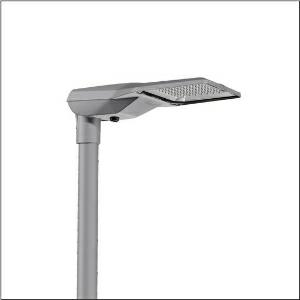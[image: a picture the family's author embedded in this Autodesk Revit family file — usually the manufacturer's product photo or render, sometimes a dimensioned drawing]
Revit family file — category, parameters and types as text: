
# Revit family: streetlight_sl_21_iq_midi___p0_5a_5xe3v31u08mb_699d
name_source: partatom
category: Lighting Fixtures
units: mm (PartAtom-declared; Revit-internal decimal feet)

## family parameters
Cut with Voids When Loaded = No
Host = Face
Light Source = No
Part Type = Normal
Room Calculation Point = No
Round Connector Dimension = Use Diameter
Shared = No

## types (1)
- --- (1 x LED, 18020 lm, 129.3 W, 3000K)
    Apparent Load = 129 VA
    CIE Flux Codes = 37 73 96 100 100
    Color Rendering = 70
    Color Temperature = 3000K
    Default Elevation = 1800 mm
    Description = Streetlight SL 21 iQ midi, mast luminaire, primary light control with lens, of PMMA, primary optical cover: cover, of toughened safety glass, transparent, light distribution: P0.5a, light emission: direct distribution, primary light characteristic: asymmetric, installation type: post-top, side-entry, LED, High Power LED, rated luminous flux: 18.020lm, luminous efficacy: 139lm/W, light colour: 730, colour temperature: 3000K, control gear: iQ-Street Remote, D4i with power reduction, control: pre-setting: logarithmic dimming characteristic, Street-Remote, Auto-Match, Temp-Guard, Lumen-Switch, Night-Set, Smart-Wire, Light-Fading, Desk-Remote (wireless, voltage-free reading and setting of iQ features in the workshop via application-optimized NFC function/RFID function), optimised constant luminous flux control (CLO 2.0), mains connection: 230..240V, AC, 50/60Hz, start of lifetime: 129W, end of service life: 142W, reduction: 56W, luminaire housing, of diecast aluminium, powder-coated, SITECO metallic grey (DB 702S), corrosivity category C5 high according to DIN EN ISO 12944, please order mast flange separately, inclination adjustable: 0°, 5°, 10°, 15°, sealing non-destructively replaceable, multi-level sealing system, length: 644mm, width: 335mm, height: 110mm, mast flange for spigot size: 42mm (side-entry): 5XC10008XM4, 60/48mm (side-entry/post-top): 5XC10108XM2, 76/60mm (side-entry/post-top): 5XC10108XM1, mounting height: 4..8m, Smart Interface below, protection rating (complete): IP66, insulation class (complete): insulation class II (safety insulation), certification: CE, ENEC, ENEC+, VDE, impact resistance: IK10, permissible operating ambient temperature for outdoor applications: -40..+50°C, standard-compliant lighting for roads and squares, packaging unit: 1 piece

Light Distribution: P0.5a
    Height = 111 mm
    Lamp = 1 x LED
    Lamp Light Flux = 18020 lm
    Lamp Power = 129.3 W
    Lamp count = 1
    Length = 644 mm
    Luminous efficacy = 139 lm/W
    Manufacturer = Siteco
    ModVariant = No
    Model = 5XE3V31U08MB
    Number of Poles = 1
    OnlyDefault = Yes
    Power Factor = 1
    Product Name = Streetlight SL 21 iQ midi | P0.5a
    Product group = mast luminaire | pylon top
    ProductGroupID = 6100
    Protection Class = Protection class II
    Protection Degree = IP 66
    RLX_Detail_Level = 1
    RLX_Emergency_Light_Flux = 0 lm
    RLX_Emergency_Type = 0
    RLX_Emergency_Type_DB = No
    RlxData = <blob elided: 90517 chars, md5=68fff909>
    Socket = socket
    Standby Power = 0 W
    System Light Flux = 18021 lm
    System Power = 129 W
    Type Comments = factory setting: luminous flux: 100 % | dim-lin: 254 | 672 mA
    Type Image = l_1004300.jpg
    URL = http://relux.com
    VarID = @adj_078259
    Voltage = 0 V
    Weight = 0.00 kg
    Width = 336 mm

## geometry (parser evidence)
native form markers: Blend x4, Sweep x11
no freeform markers — native parametric forms only
